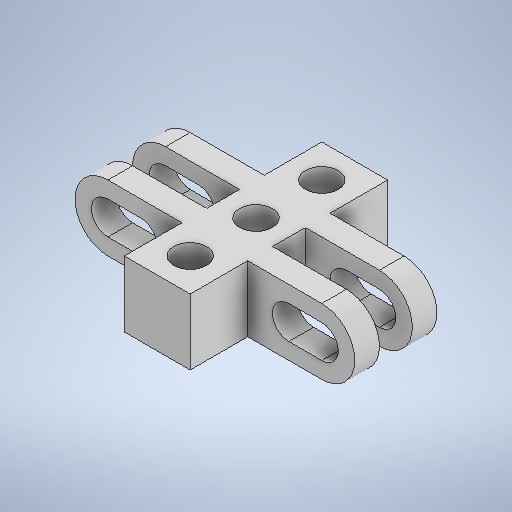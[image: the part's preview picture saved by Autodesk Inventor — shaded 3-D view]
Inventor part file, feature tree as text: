
AUTODESK INVENTOR PART (.ipt)
format: ipt  version: 2025.1 (Build 291241000, 241)  size: 341,504 bytes
history: native  units: mm
features: sketch x5, extrude x2, mirror x2, plane x1, hole x1
ambient origin geometry x8: Origin, YZ Plane, XZ Plane, XY Plane, X Axis, Y Axis, Z Axis, Center Point
bodies: Solid1 (feature_tree)
feature tree (11):
  extrude  "Extrusion1"  Depth=24.0mm
  plane  "Work Plane1"
  extrude  "Extrusion2"  [1 undecoded]
  mirror  "Mirror1"
  mirror  "Mirror2"
  hole  "Hole1"  [1 undecoded]
  sketch  "Sketch5"  dims[d10=4.0mm]
  sketch  "Sketch6"  dims[d11=2.0mm d12=3.0mm d13=0.0mm d14=8.0mm d15=8.0mm d16=4.0mm d17=6.0mm d18=4.0mm d19=2.0mm d20=90.0deg d21=4.0mm d22=0.0mm d25=4.0mm d26=5.0mm d28=4.0mm d31=5.0mm]
  sketch  "Sketch1"  dims[d0=8.0mm d1=24.0mm]
  sketch  "Sketch3"  dims[d2=8.0mm d3=0.0mm d7=-2.0mm]
  sketch  "Sketch4"  dims[d8=4.0mm d9=9.0mm]
note: 2 required parameter values undecoded (feature->parameter linkage not recoverable at this tier; creation-order binding heuristic only, values carry confidence <= 0.55)
